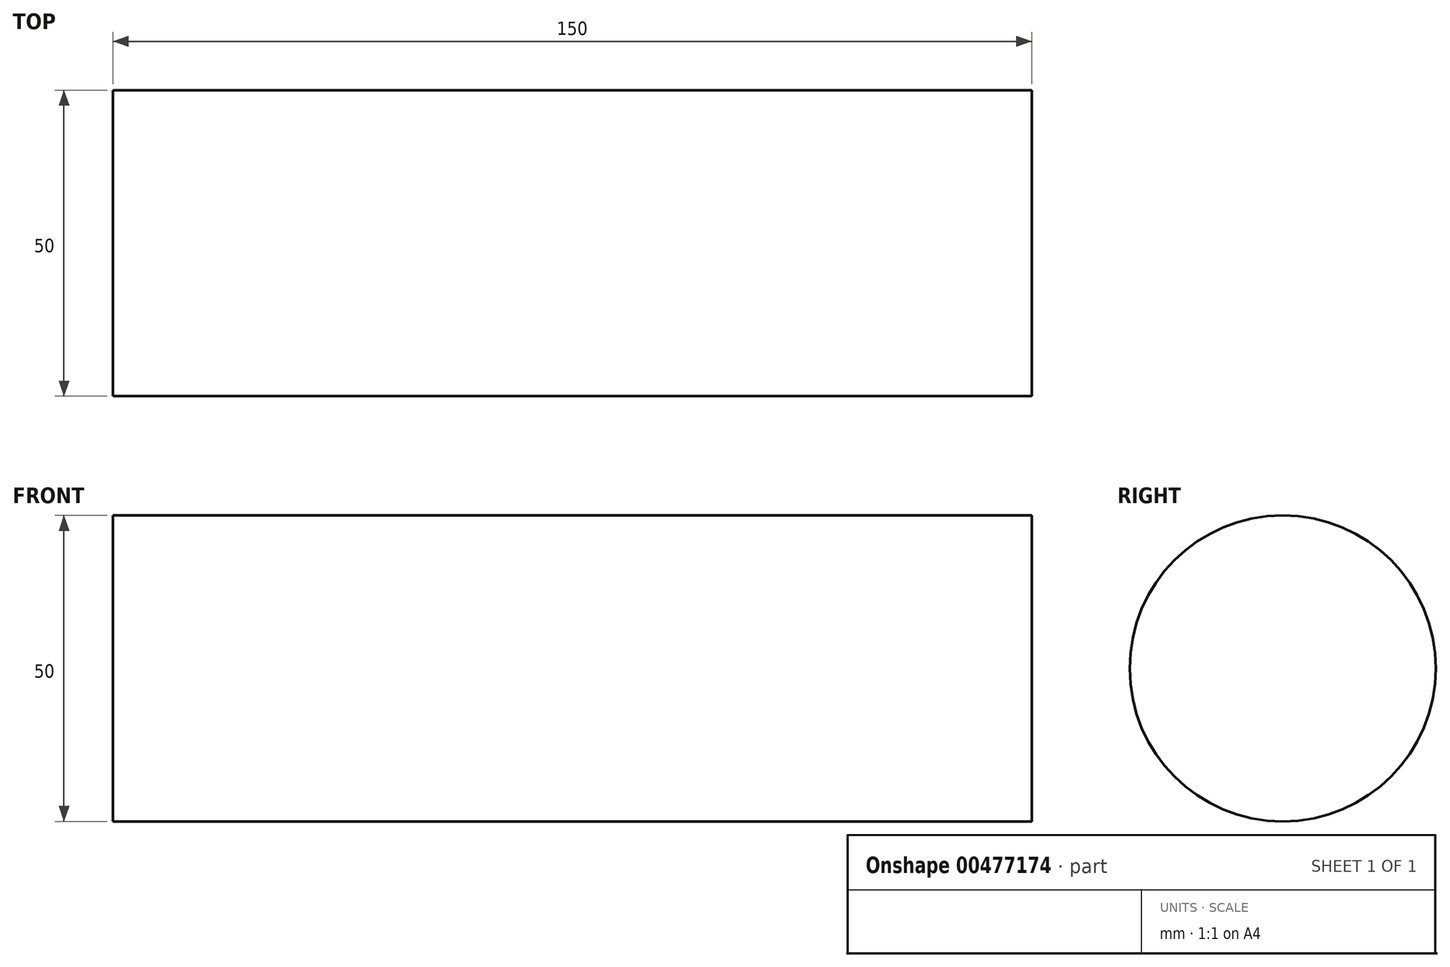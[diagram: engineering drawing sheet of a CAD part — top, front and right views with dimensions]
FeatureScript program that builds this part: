
annotation { "Feature Type Name" : "Feature", "Feature Type Description" : "" }
export const myFeature = defineFeature(function(context is Context, id is Id, definition is map)
    precondition{}
    {
        {
            var Q0;
            Q0=qCreatedBy(makeId("Right.planeOp"),FACE);
            var sketch = newSketch(context, id + "F0", { "sketchPlane" : qUnion([Q0])});
            skCircle(sketch, "E0", {"center": v(0, 0) * mm, "radius": 25 * mm});
            skSolve(sketch);
        }
        {
            var Q0;
            Q0=makeQuery(id+"F0.imprint","IMPRINT",FACE,{"disambiguationData":[TD([[makeQuery(id+"F0.imprint","IMPRINT",EDGE,{"derivedFrom":sQuery(id+"F0.wireOp",EDGE,"E0")}),1.0]])]});
            extrude(context, id + "F1", {"entities" : qUnion([Q0]), "depth" : 150 * mm});
        }
    });
